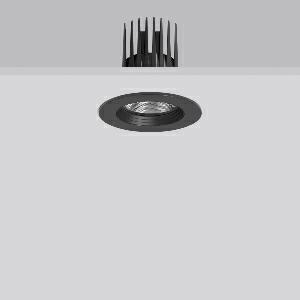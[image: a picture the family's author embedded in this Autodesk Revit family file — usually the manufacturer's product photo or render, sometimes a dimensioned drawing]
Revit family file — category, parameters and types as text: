
# Revit family: heledon_mini_e_901741_003_1_1797
name_source: partatom
category: Lighting Fixtures
units: mm (PartAtom-declared; Revit-internal decimal feet)

## family parameters
Cut with Voids When Loaded = No
Host = Face
Light Source = No
Part Type = Normal
Room Calculation Point = No
Round Connector Dimension = Use Diameter
Shared = No

## types (1)
- HELEDON mini E (1 x LED Modul 940, 2600 lm, 4000)
    Apparent Load = 20 VA
    Approval mark = CE
    CIE Flux Codes = 99 100 100 100 100
    Color Rendering = 92
    Color Temperature = 4000
    Default Elevation = 1800 mm
    Description = Series: HELEDON mini
Round recessed downlight. Housing: die-cast aluminium, powder-coated. Black plastic ring and recessed LED to prevent glare from the side. Optical assembly with reflector made of MIRO-Silver with 98% total light reflection for outstanding efficiency - can be changed without tools. Best colour rendering index Ra>90. Suitable for Recessed ceiling mounting. Installation without tools thanks to spring fastening system. Including separate LED converter with connecting cable 600 mm.High quality converter without flickering and stroboscopic effect. Through-wiring box (5 pole) available as accessory. The following accessories can be mounted without use of tools: interchangeable lenses, decorative glasses, honeycomb louvre, clear and frosted diffusers, white interchangeable plastic ring. 
Colour: deep black, matt (RAL 9005)
Diameter: 124 mm
Height: 3 mm
Cut-out diameter: 114 mm
Recess height: 170 mm
Luminaire: recess height: 120 mm
Lamp: LED
Socket: without socket
Colour temperature: 4000K
Colour rendering index (CRI): 92
System power: 20 W
Rated luminous flux: 2600 lm
Luminous efficiency: 130 lm/W
Control gear: Regulated power supply
Protection class: II
Type of protection: IP 20
    Height = 0 mm  [stored 0 ft]
    Lamp = 1 x LED Modul 940
    Lamp Light Flux = 2600 lm
    Lamp count = 1
    Length = 124 mm  [stored 0.406824 ft]
    Lifetime = 50000 h
    Luminous efficacy = 130 lm/W
    Manufacturer = RZB
    ModVariant = No
    Model = 901741.003.1
    Mounting Place = Ceiling
    Mounting Type = Recessed
    Number of Poles = 1
    OnlyDefault = Yes
    Power Factor = 1
    Product Name = HELEDON mini E
    Product group = Recessed downlights
    ProductGroupID = 402
    Protection Class = Protection class II
    Protection Degree = IP 20
    RLX_Detail_Level = 1
    RLX_Emergency_Light_Flux = 0 lm
    RLX_Emergency_Type = 0
    RLX_Emergency_Type_DB = No
    RlxData = <blob elided: 128937 chars, md5=bb40b6e5>
    Socket = socket
    Standby Power = 0 W
    System Light Flux = 2600 lm
    System Power = 20 W
    Type Comments = Product without accessories
    Type Image = 901657.003.jpg
    URL = http://relux.com
    VarID = ---
    Voltage = 230 V
    Voltage Range = 220-240 V
    Weight = 0.00 kg
    Width = 0 mm  [stored 0 ft]

note: [stored X ft] marks values corroborated as IEEE doubles in the binary element streams (Revit-internal decimal feet)

## geometry (parser evidence)
native form markers: Blend x4, Sweep x9
no freeform markers — native parametric forms only
